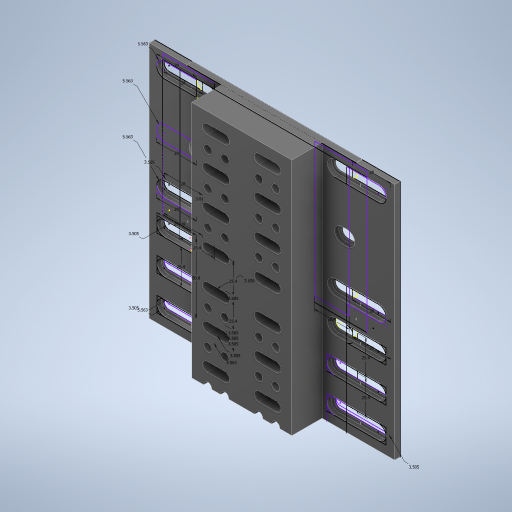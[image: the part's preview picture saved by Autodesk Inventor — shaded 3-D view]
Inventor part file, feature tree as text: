
AUTODESK INVENTOR PART (.ipt)
format: ipt  version: 2024.2 (Build 282272000, 272)  size: 1,240,064 bytes
history: native  units: in
note: dims shown in document units (in); Inventor stores cm internally (conversion verified against a paired STEP export)
features: extrude x9, sketch x7, direct_edit x6, other x4, move_body x4, thicken_offset x2, mirror x1
ambient origin geometry x8: Origin, YZ Plane, XZ Plane, XY Plane, X Axis, Y Axis, Z Axis, Center Point
bodies: Solid1 (feature_tree)
feature tree (33):
  other  "LS-5012 - LS-BREADBOARD ADAPTER PLATE (CATALOG MODEL).SAT"
  sketch  "Sketch1"  dims[d0=1.0in d1=1.0in]
  extrude  "Extrusion1"  Depth=1.0in
  thicken_offset  "Thicken1"
  direct_edit  "Direct Edit3"
  mirror  "Mirror3"
  extrude  "Extrusion5"  Depth=0.1in
  extrude  "Extrusion6"  Depth=0.01in TaperAngle=0.0deg
  sketch  "Sketch6"  dims[d28=0.956in d29=0.0in d30=0.175in d31=0.0in]
  extrude  "Extrusion7"  Depth=0.175in TaperAngle=0.0deg
  sketch  "Sketch7"  dims[d32=1.1024in d33=1.1024in]
  extrude  "Extrusion8"  Depth=1.1024in
  direct_edit  "Direct Edit6"
  direct_edit  "Direct Edit7"
  direct_edit  "Direct Edit8"
  extrude  "Extrusion9"  Depth=1.1024in
  thicken_offset  "Thicken2"
  direct_edit  "Direct Edit9"
  extrude  "Extrusion10"  Depth=0.138in
  extrude  "Extrusion11"  Depth=1.1024in
  extrude  "Extrusion12"  Depth=1.1024in
  direct_edit  "Direct Edit10"
  sketch  "Sketch9"  dims[d36=0.15in d37=0.138in d38=1.1024in d39=1.1024in d40=1.0in d41=1.0in d42=1.0in d43=1.0in d44=0.138in d45=0.138in d46=0.138in d47=0.138in d48=0.138in d49=0.138in d50=0.138in d51=0.175in d52=0.0in d53=1.1417in d54=0.219in d55=1.1417in d56=1.1417in d57=0.7874in d59=1.0in d60=0.3937in d62=1.0in d64=0.138in d65=0.138in d66=0.7874in d68=2.0in d69=0.3937in d71=1.0in d73=0.219in d74=0.219in d75=0.06in d76=0.0in d77=0.219in d80=-0.0787in d81=0.563in d82=0.0in d83=0.0in d84=-0.0066in d85=1.1024in d86=0.1575in d87=0.0in d88=0.0394in d89=0.0394in d90=0.0612in d91=0.1969in d92=0.0in d93=0.1378in d94=0.0in d95=0.1378in d96=0.0in d97=0.0in d98=0.0in d99=-0.0394in d101=0.7874in d103=0.3937in d105=0.7874in d107=0.3937in d108=1.1417in d109=0.219in]
  sketch  "Sketch4"  dims[d2=0.2in d3=0.0in d14=0.1in d15=3.0in]
  sketch  "Sketch5"  dims[d22=0.0in d23=0.0in d24=0.0345in d25=0.0in d26=0.0in d27=0.01in]
  sketch  "Sketch8"  dims[d34=1.1024in d35=1.1024in]
  move_body  "Move3"
  move_body  "Move4"
  other  "Size3"
  other  "Size4"
  move_body  "Move5"
  other  "Size5"
  move_body  "Move6"
